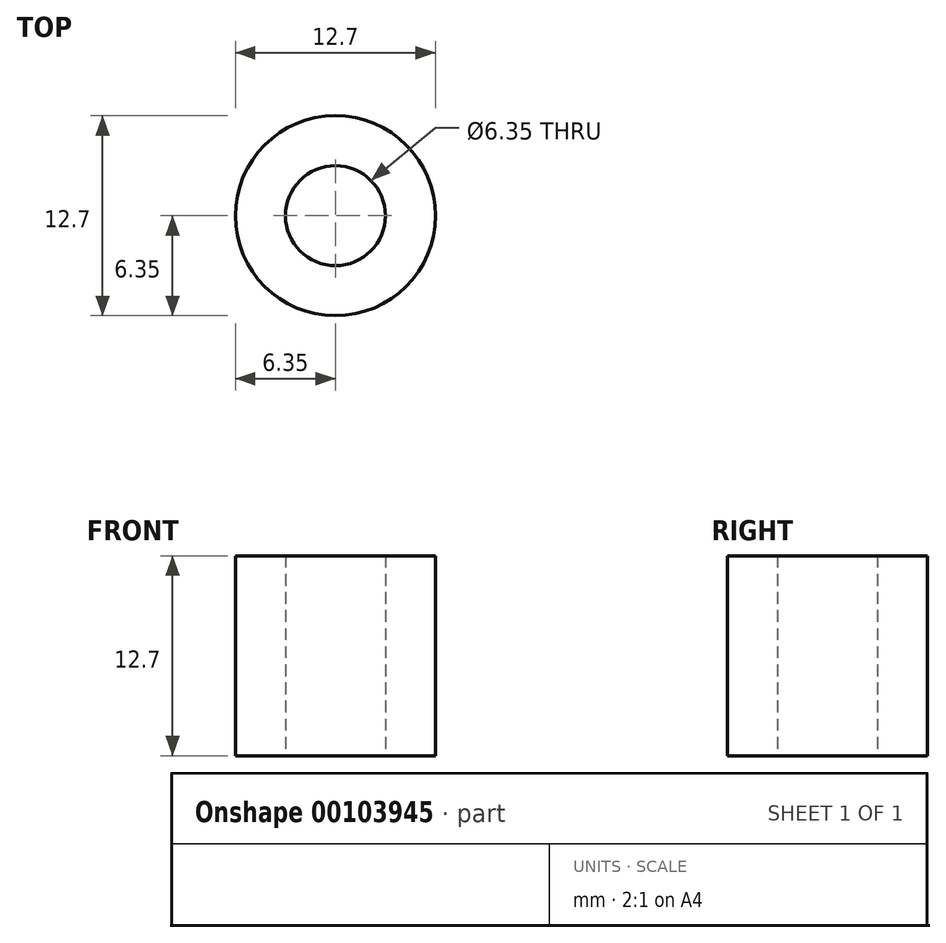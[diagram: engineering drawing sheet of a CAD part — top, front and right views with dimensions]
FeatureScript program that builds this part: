
annotation { "Feature Type Name" : "Feature", "Feature Type Description" : "" }
export const myFeature = defineFeature(function(context is Context, id is Id, definition is map)
    precondition{}
    {
        {
            var Q0;
            Q0=qCreatedBy(makeId("Top.planeOp"),FACE);
            var sketch = newSketch(context, id + "F0", { "sketchPlane" : qUnion([Q0])});
            skCircle(sketch, "E0", {"center": v(0, 0) * mm, "radius": 6.35 * mm});
            skCircle(sketch, "E1", {"center": v(0, 0) * mm, "radius": 3.18 * mm});
            skSolve(sketch);
        }
        {
            var Q0;
            Q0=qSketchRegion(id+"F0",true);
            extrude(context, id + "F1", {"entities" : qUnion([Q0]), "depth" : 12.7 * mm});
        }
    });
